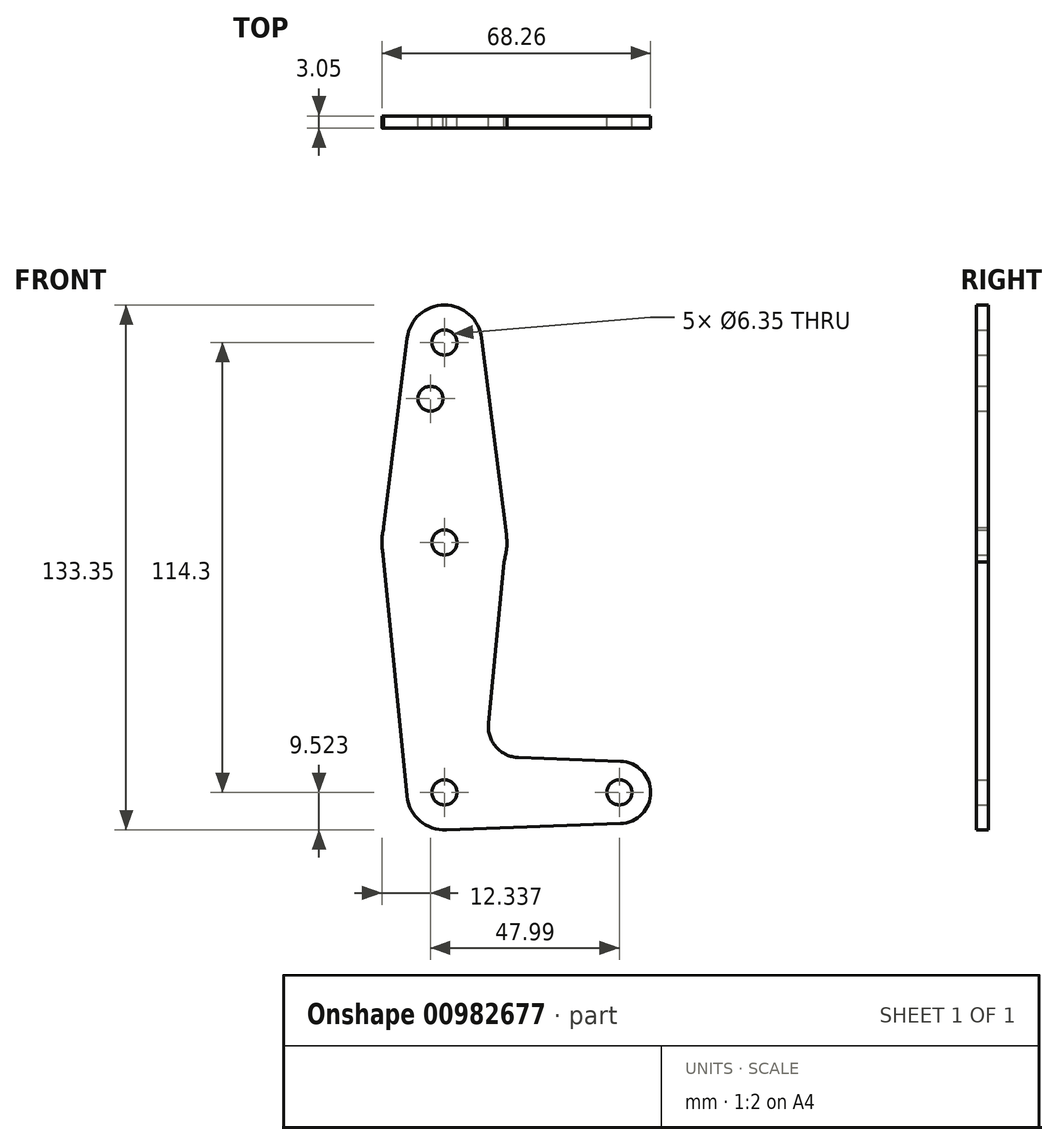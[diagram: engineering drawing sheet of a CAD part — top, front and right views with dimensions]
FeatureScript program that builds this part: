
annotation { "Feature Type Name" : "Feature", "Feature Type Description" : "" }
export const myFeature = defineFeature(function(context is Context, id is Id, definition is map)
    precondition{}
    {
        {
            var Q0;
            Q0=qCreatedBy(makeId("Front.planeOp"),FACE);
            var sketch = newSketch(context, id + "F0", { "sketchPlane" : qUnion([Q0])});
            skLineSegment(sketch, "E0", {"start": v(-33.93, 60.72) * mm, "end": v(-33.93, -53.58) * mm, "construction": true});
            skLineSegment(sketch, "E1", {"start": v(-33.93, -53.58) * mm, "end": v(10.52, -53.58) * mm, "construction": true});
            skCircle(sketch, "E2", {"center": v(-33.93, 60.72) * mm, "radius": 9.53 * mm});
            skCircle(sketch, "E3", {"center": v(-33.93, 9.92) * mm, "radius": 15.88 * mm});
            skCircle(sketch, "E4", {"center": v(-33.93, -53.58) * mm, "radius": 9.53 * mm});
            skCircle(sketch, "E5", {"center": v(10.52, -53.58) * mm, "radius": 7.94 * mm});
            skLineSegment(sketch, "E6", {"start": v(-43.39, 61.9) * mm, "end": v(-49.8, 10.04) * mm});
            skLineSegment(sketch, "E7", {"start": v(-49.8, 10.04) * mm, "end": v(-43.41, -54.52) * mm});
            skLineSegment(sketch, "E8", {"start": v(-24.48, 61.91) * mm, "end": v(-18.18, 11.9) * mm});
            skLineSegment(sketch, "E9", {"start": v(-18.18, 11.9) * mm, "end": v(-22.74, -36.02) * mm});
            skLineSegment(sketch, "E10", {"start": v(-15.1, -44.72) * mm, "end": v(10.8, -45.64) * mm});
            skLineSegment(sketch, "E11", {"start": v(-33.43, -63.09) * mm, "end": v(10.8, -61.5) * mm});
            skCircle(sketch, "E12", {"center": v(-33.93, 60.72) * mm, "radius": 3.18 * mm});
            skCircle(sketch, "E13", {"center": v(-33.93, 9.92) * mm, "radius": 3.18 * mm});
            skCircle(sketch, "E14", {"center": v(-33.93, -53.58) * mm, "radius": 3.18 * mm});
            skCircle(sketch, "E15", {"center": v(10.52, -53.58) * mm, "radius": 3.18 * mm});
            skCircle(sketch, "E16", {"center": v(-37.47, 46.45) * mm, "radius": 3.18 * mm});
            skArc(sketch, "E17.filletArc", {"start": v(-22.74, -36.02) * mm, "mid": v(-20.8, -42.02) * mm, "end": v(-15.1, -44.72) * mm});
            skSolve(sketch);
        }
        {
            var Q0;
            Q0 = qSketchRegion(id + "F0", true);
            extrude(context, id + "F1", {"entities" : qUnion([Q0]), "depth" : 3.05 * mm, "offsetDistance" : 25.4 * mm});
        }
    });
